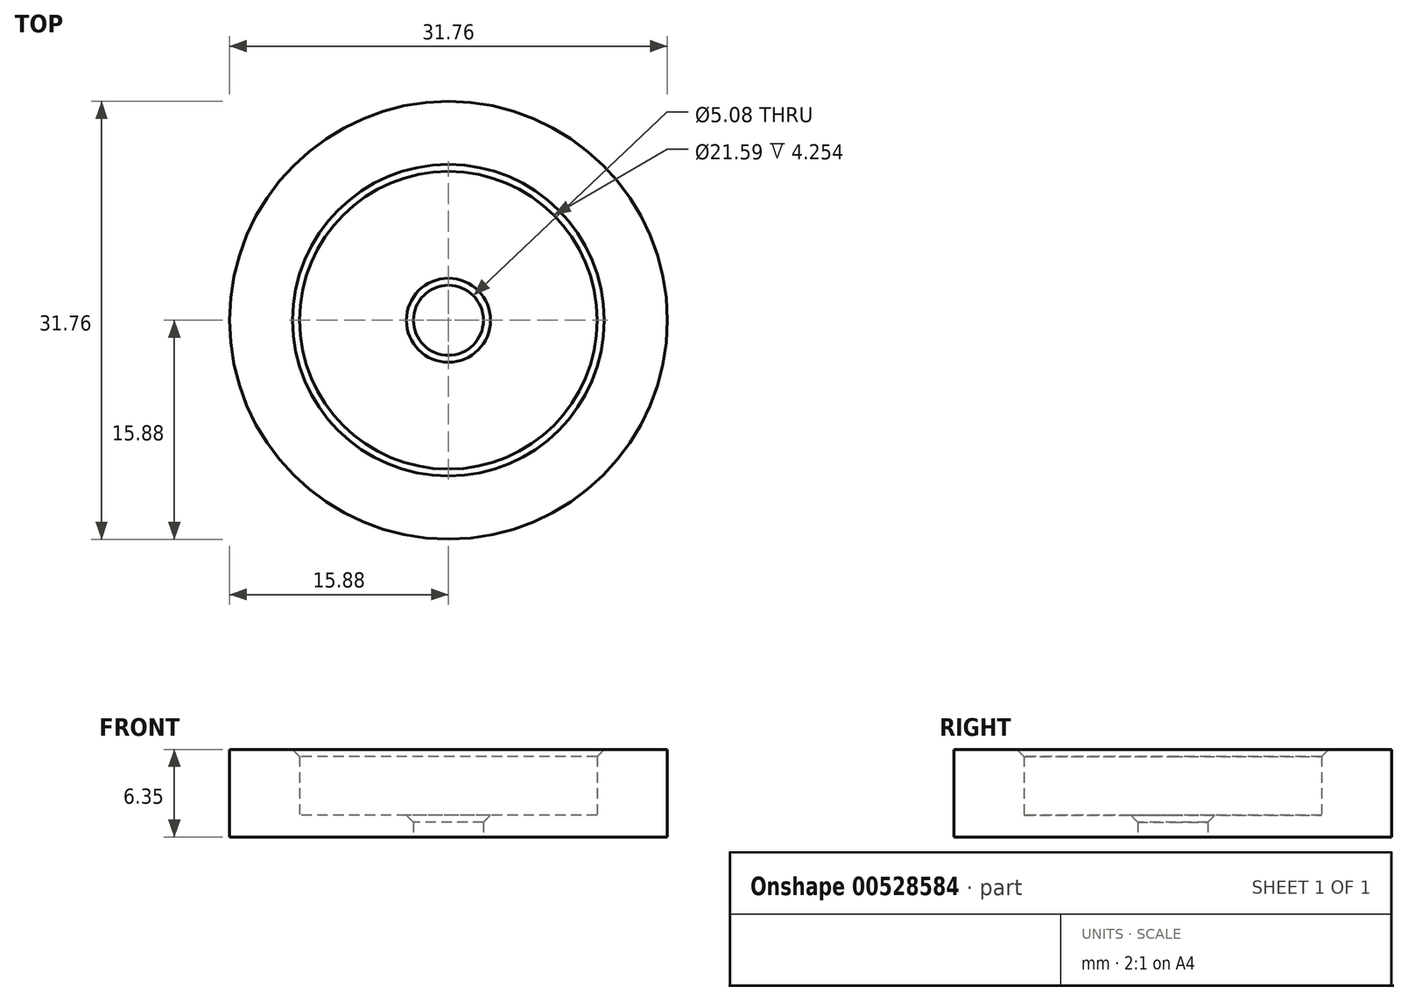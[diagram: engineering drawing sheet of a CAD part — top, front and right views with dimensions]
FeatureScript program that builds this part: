
annotation { "Feature Type Name" : "Feature", "Feature Type Description" : "" }
export const myFeature = defineFeature(function(context is Context, id is Id, definition is map)
    precondition{}
    {
        {
            var Q0;
            Q0=qCreatedBy(makeId("Top.planeOp"),FACE);
            var sketch = newSketch(context, id + "F0", { "sketchPlane" : qUnion([Q0])});
            skCircle(sketch, "E0", {"center": v(0, 0) * mm, "radius": 2.54 * mm});
            skCircle(sketch, "E1", {"center": v(0, 0) * mm, "radius": 15.88 * mm});
            skSolve(sketch);
        }
        {
            var Q0;
            Q0=makeQuery(id+"F0.imprint","IMPRINT",FACE,{"disambiguationData":[TD([[makeQuery(id+"F0.imprint","IMPRINT",EDGE,{"derivedFrom":sQuery(id+"F0.wireOp",EDGE,"E0")}),-1.0]])]});
            extrude(context, id + "F1", {"entities" : qUnion([Q0]), "depth" : 1.59 * mm, "offsetDistance" : 25.4 * mm});
        }
        {
            var Q0;
            Q0=makeQuery(id+"F1.opExtrude","CAP_FACE",FACE,{"disambiguationData":[OSD([sQuery(id+"F0.wireOp",EDGE,"E0"),sQuery(id+"F0.wireOp",EDGE,"E1")])],"isStart":false});
            var sketch = newSketch(context, id + "F2", { "sketchPlane" : qUnion([Q0])});
            skCircle(sketch, "E2.0", {"center": v(0, 0) * mm, "radius": 15.88 * mm});
            skCircle(sketch, "E3", {"center": v(0, 0) * mm, "radius": 10.8 * mm});
            skSolve(sketch);
        }
        {
            var Q0;
            Q0=makeQuery(id+"F2.imprint","IMPRINT",FACE,{"disambiguationData":[TD([[makeQuery(id+"F2.imprint","IMPRINT",EDGE,{"derivedFrom":sQuery(id+"F2.wireOp",EDGE,"E2.0")}),1.0]])]});
            extrude(context, id + "F3", {"entities" : qUnion([Q0]), "operationType" : NewBodyOperationType.ADD, "depth" : 4.76 * mm, "offsetDistance" : 25.4 * mm});
        }
        {
            var Q0;
            Q0=makeQuery(id+"F3.opExtrude","CAP_EDGE",EDGE,{"disambiguationData":[OSD([sQuery(id+"F2.wireOp",EDGE,"E3")])],"isStart":false});
            var Q1;
            Q1=makeQuery(id+"F1.opExtrude","CAP_EDGE",EDGE,{"disambiguationData":[OSD([sQuery(id+"F0.wireOp",EDGE,"E0")])],"isStart":false});
            chamfer(context, id + "F4", {"entities" : qUnion([Q0, Q1]), "width" : 0.5 * mm, "tangentPropagation" : true});
        }
    });
